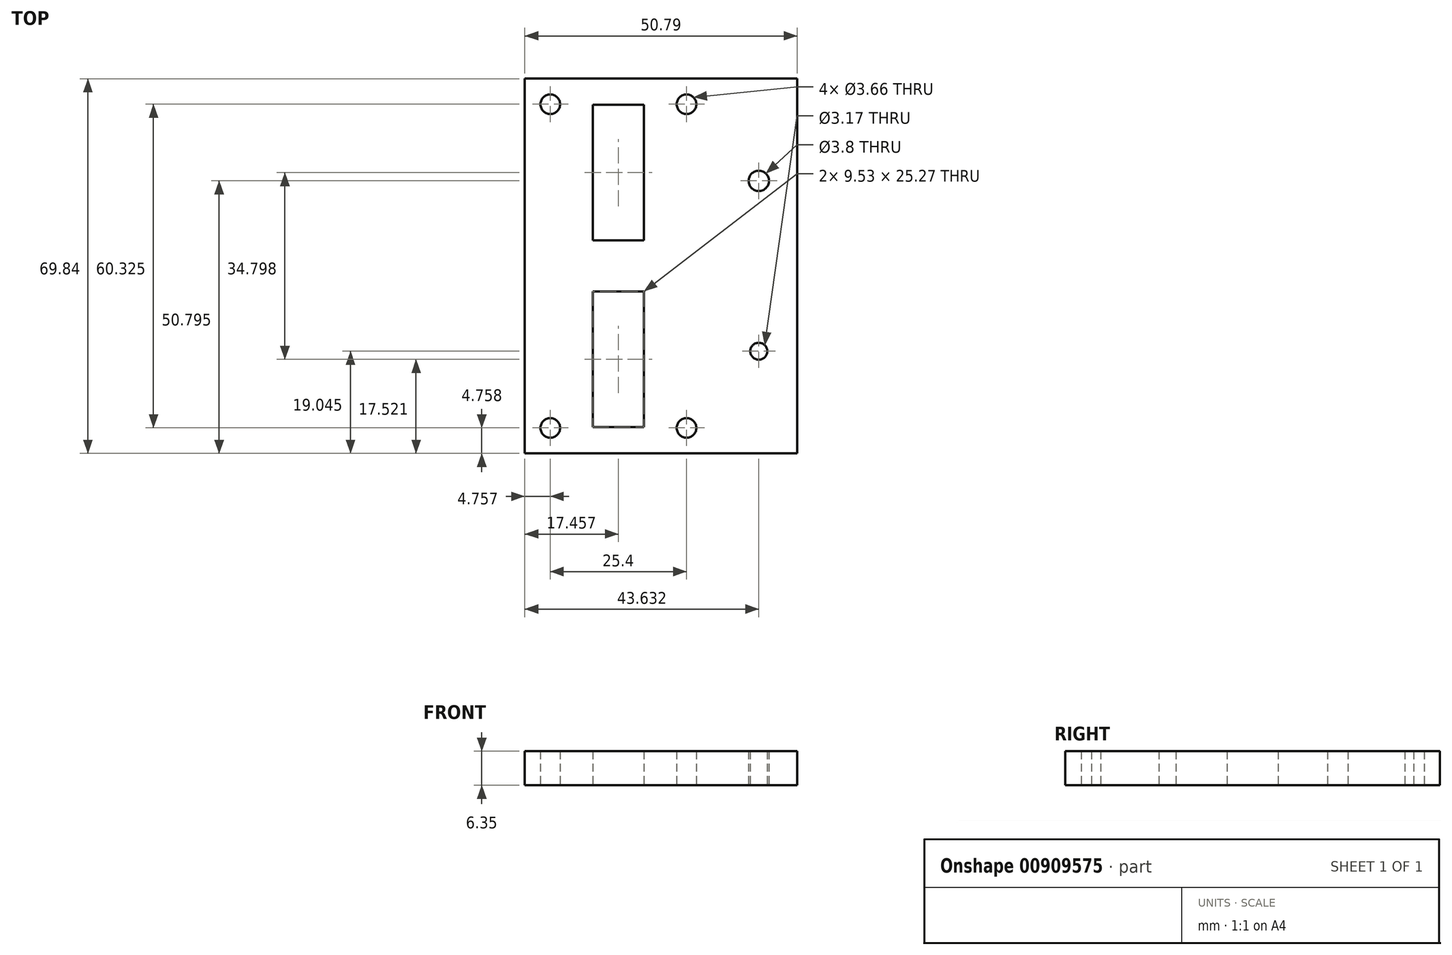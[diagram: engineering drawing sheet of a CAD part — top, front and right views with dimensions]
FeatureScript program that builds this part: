
annotation { "Feature Type Name" : "Feature", "Feature Type Description" : "" }
export const myFeature = defineFeature(function(context is Context, id is Id, definition is map)
    precondition{}
    {
        {
            var Q0;
            Q0=qCreatedBy(makeId("Top.planeOp"),FACE);
            var sketch = newSketch(context, id + "F0", { "sketchPlane" : qUnion([Q0])});
            skLineSegment(sketch, "E0.bottom", {"start": v(-152.4, 152.4) * mm, "end": v(152.4, 152.4) * mm});
            skLineSegment(sketch, "E0.top", {"start": v(-152.4, -152.4) * mm, "end": v(152.4, -152.4) * mm});
            skLineSegment(sketch, "E0.left", {"start": v(-152.4, 152.4) * mm, "end": v(-152.4, -152.4) * mm});
            skLineSegment(sketch, "E0.right", {"start": v(152.4, 152.4) * mm, "end": v(152.4, -152.4) * mm});
            skPoint(sketch, "E0.middle", {"position": v(0, 0) * mm});
            skLineSegment(sketch, "E1.0", {"start": v(-107.95, -82.55) * mm, "end": v(107.95, -82.55) * mm});
            skLineSegment(sketch, "E2.0", {"start": v(-107.95, 107.95) * mm, "end": v(-107.95, -82.55) * mm});
            skLineSegment(sketch, "E3", {"start": v(0, 152.4) * mm, "end": v(0, -152.4) * mm, "construction": true});
            skLineSegment(sketch, "E4", {"start": v(-152.4, 0) * mm, "end": v(152.4, 0) * mm, "construction": true});
            skLineSegment(sketch, "E5.MirrorCS", {"start": v(107.95, 107.95) * mm, "end": v(107.95, -82.55) * mm});
            skLineSegment(sketch, "E6.0", {"start": v(-107.95, 107.95) * mm, "end": v(107.95, 107.95) * mm});
            skLineSegment(sketch, "E7.bottom", {"start": v(-104.78, 34.93) * mm, "end": v(-53.98, 34.93) * mm});
            skLineSegment(sketch, "E7.top", {"start": v(-104.78, -34.92) * mm, "end": v(-53.98, -34.92) * mm});
            skLineSegment(sketch, "E7.left", {"start": v(-104.78, 34.92) * mm, "end": v(-104.78, -34.92) * mm});
            skLineSegment(sketch, "E7.right", {"start": v(-69.85, 34.92) * mm, "end": v(-69.85, -34.92) * mm});
            skLineSegment(sketch, "E8", {"start": v(-87.31, 34.92) * mm, "end": v(-87.31, -152.4) * mm, "construction": true});
            skLineSegment(sketch, "E9.bottom", {"start": v(-82.55, 4.76) * mm, "end": v(-92.08, 4.76) * mm});
            skLineSegment(sketch, "E9.top", {"start": v(-82.55, 30.04) * mm, "end": v(-92.08, 30.04) * mm});
            skLineSegment(sketch, "E9.left", {"start": v(-82.55, 4.76) * mm, "end": v(-82.55, 30.04) * mm});
            skLineSegment(sketch, "E9.right", {"start": v(-92.08, 4.76) * mm, "end": v(-92.08, 30.04) * mm});
            skPoint(sketch, "E9.middle", {"position": v(-87.31, 17.4) * mm});
            skPoint(sketch, "E10", {"position": v(-69.85, 0) * mm});
            skLineSegment(sketch, "E11.MirrorCS", {"start": v(-92.08, -4.76) * mm, "end": v(-92.08, -30.04) * mm});
            skLineSegment(sketch, "E12.MirrorCS", {"start": v(-82.55, -4.76) * mm, "end": v(-82.55, -30.04) * mm});
            skPoint(sketch, "E13.MirrorP", {"position": v(-87.31, -17.4) * mm});
            skLineSegment(sketch, "E14.MirrorCS", {"start": v(-82.55, -4.76) * mm, "end": v(-92.08, -4.76) * mm});
            skLineSegment(sketch, "E15.MirrorCS", {"start": v(-82.55, -30.04) * mm, "end": v(-92.08, -30.04) * mm});
            skCircle(sketch, "E16", {"center": v(-101.6, -127) * mm, "radius": 11.43 * mm});
            skCircle(sketch, "E17", {"center": v(-86.1, -111.5) * mm, "radius": 1.59 * mm});
            skCircle(sketch, "E18.1.0", {"center": v(-117.1, -111.5) * mm, "radius": 1.59 * mm});
            skCircle(sketch, "E18.2.0", {"center": v(-117.1, -142.5) * mm, "radius": 1.59 * mm});
            skCircle(sketch, "E18.3.0", {"center": v(-86.1, -142.5) * mm, "radius": 1.59 * mm});
            skCircle(sketch, "E19.MirrorC", {"center": v(117.1, -111.5) * mm, "radius": 1.59 * mm});
            skCircle(sketch, "E20.MirrorC", {"center": v(86.1, -111.5) * mm, "radius": 1.59 * mm});
            skCircle(sketch, "E21.MirrorC", {"center": v(117.1, -142.5) * mm, "radius": 1.59 * mm});
            skPoint(sketch, "E22.MirrorP", {"position": v(101.6, -127) * mm});
            skCircle(sketch, "E23.MirrorC", {"center": v(86.1, -142.5) * mm, "radius": 1.59 * mm});
            skCircle(sketch, "E24.MirrorC", {"center": v(101.6, -127) * mm, "radius": 11.43 * mm});
            skPoint(sketch, "E25.orphan", {"position": v(-87.31, -34.92) * mm});
            skCircle(sketch, "E26", {"center": v(-103.19, -89.7) * mm, "radius": 1.59 * mm});
            skCircle(sketch, "E27.MirrorC", {"center": v(-71.44, -89.7) * mm, "radius": 1.59 * mm});
            skLineSegment(sketch, "E28.bottom", {"start": v(-96.84, -82.55) * mm, "end": v(-77.79, -82.55) * mm});
            skLineSegment(sketch, "E28.top", {"start": v(-96.84, -96.85) * mm, "end": v(-77.79, -96.85) * mm});
            skLineSegment(sketch, "E28.left", {"start": v(-96.84, -82.55) * mm, "end": v(-96.84, -96.85) * mm});
            skLineSegment(sketch, "E28.right", {"start": v(-77.79, -82.55) * mm, "end": v(-77.79, -96.85) * mm});
            skPoint(sketch, "E29", {"position": v(-87.31, -96.85) * mm});
            skLineSegment(sketch, "E30.MirrorCS", {"start": v(96.84, -82.55) * mm, "end": v(96.84, -96.85) * mm});
            skCircle(sketch, "E31.MirrorC", {"center": v(71.44, -89.7) * mm, "radius": 1.59 * mm});
            skCircle(sketch, "E32.MirrorC", {"center": v(103.19, -89.7) * mm, "radius": 1.59 * mm});
            skLineSegment(sketch, "E33.MirrorCS", {"start": v(96.84, -82.55) * mm, "end": v(77.79, -82.55) * mm});
            skPoint(sketch, "E34.MirrorP", {"position": v(87.31, -96.85) * mm});
            skLineSegment(sketch, "E35.MirrorCS", {"start": v(77.79, -82.55) * mm, "end": v(77.79, -96.85) * mm});
            skLineSegment(sketch, "E36.MirrorCS", {"start": v(96.84, -96.85) * mm, "end": v(77.79, -96.85) * mm});
            skCircle(sketch, "E37.MirrorC", {"center": v(-103.3, 114.85) * mm, "radius": 1.59 * mm});
            skLineSegment(sketch, "E38.MirrorCS", {"start": v(-96.97, 122) * mm, "end": v(-77.92, 122.03) * mm});
            skLineSegment(sketch, "E39.MirrorCS", {"start": v(-96.95, 107.7) * mm, "end": v(-77.9, 107.73) * mm});
            skCircle(sketch, "E40.MirrorC", {"center": v(103.07, 115.1) * mm, "radius": 1.59 * mm});
            skLineSegment(sketch, "E41.MirrorCS", {"start": v(-96.95, 107.7) * mm, "end": v(-96.97, 122) * mm});
            skCircle(sketch, "E42.MirrorC", {"center": v(-71.56, 114.89) * mm, "radius": 1.59 * mm});
            skLineSegment(sketch, "E43.MirrorCS", {"start": v(96.7, 122.24) * mm, "end": v(77.66, 122.21) * mm});
            skCircle(sketch, "E44.MirrorC", {"center": v(71.32, 115.06) * mm, "radius": 1.59 * mm});
            skLineSegment(sketch, "E45.MirrorCS", {"start": v(96.73, 107.94) * mm, "end": v(77.68, 107.91) * mm});
            skPoint(sketch, "E46.MirrorP", {"position": v(-87.44, 122.02) * mm});
            skPoint(sketch, "E47.MirrorP", {"position": v(87.18, 122.23) * mm});
            skLineSegment(sketch, "E48.MirrorCS", {"start": v(-108.06, 107.7) * mm, "end": v(107.84, 107.95) * mm});
            skLineSegment(sketch, "E49.MirrorCS", {"start": v(77.68, 107.91) * mm, "end": v(77.66, 122.21) * mm});
            skLineSegment(sketch, "E50.MirrorCS", {"start": v(-77.9, 107.73) * mm, "end": v(-77.92, 122.03) * mm});
            skLineSegment(sketch, "E51.MirrorCS", {"start": v(96.73, 107.94) * mm, "end": v(96.7, 122.24) * mm});
            skLineSegment(sketch, "E52.0", {"start": v(-53.97, 34.92) * mm, "end": v(-53.98, -34.92) * mm});
            skCircle(sketch, "E53", {"center": v(-61.14, 15.87) * mm, "radius": 1.59 * mm});
            skCircle(sketch, "E54", {"center": v(-100.01, 30.16) * mm, "radius": 1.83 * mm});
            skCircle(sketch, "E55.MirrorC", {"center": v(-100.01, -30.16) * mm, "radius": 1.83 * mm});
            skCircle(sketch, "E56.MirrorC", {"center": v(-74.61, 30.16) * mm, "radius": 1.83 * mm});
            skCircle(sketch, "E57.MirrorC", {"center": v(-74.61, -30.16) * mm, "radius": 1.83 * mm});
            skCircle(sketch, "E58.MirrorC", {"center": v(-61.14, -15.87) * mm, "radius": 1.59 * mm});
            skSolve(sketch);
        }
        {
            var Q0;
            {var subQ1=sQuery(id+"F0.wireOp",EDGE,"E7.right");Q0=makeQuery(id+"F0.imprint","IMPRINT",FACE,{"disambiguationData":[TD([[makeQuery(id+"F0.imprint","IMPRINT",EDGE,{"derivedFrom":subQ1}),1.0]])]});}
            var Q1;
            {var subQ0=sQuery(id+"F0.wireOp",EDGE,"E7.left");Q1=makeQuery(id+"F0.imprint","IMPRINT",FACE,{"disambiguationData":[TD([[makeQuery(id+"F0.imprint","IMPRINT",EDGE,{"derivedFrom":subQ0}),1.0]])]});}
            var Q2;
            Q2=makeQuery(id+"F0.imprint","IMPRINT",FACE,{"disambiguationData":[TD([[makeQuery(id+"F0.imprint","IMPRINT",EDGE,{"derivedFrom":sQuery(id+"F0.wireOp",EDGE,"E55.MirrorC")}),-1.0]])]});
            var Q3;
            Q3=makeQuery(id+"F0.imprint","IMPRINT",FACE,{"disambiguationData":[TD([[makeQuery(id+"F0.imprint","IMPRINT",EDGE,{"derivedFrom":sQuery(id+"F0.wireOp",EDGE,"E54")}),1.0]])]});
            var Q4;
            Q4=makeQuery(id+"F0.imprint","IMPRINT",FACE,{"disambiguationData":[TD([[makeQuery(id+"F0.imprint","IMPRINT",EDGE,{"derivedFrom":sQuery(id+"F0.wireOp",EDGE,"E56.MirrorC")}),-1.0]])]});
            var Q5;
            Q5=makeQuery(id+"F0.imprint","IMPRINT",FACE,{"disambiguationData":[TD([[makeQuery(id+"F0.imprint","IMPRINT",EDGE,{"derivedFrom":sQuery(id+"F0.wireOp",EDGE,"E57.MirrorC")}),1.0]])]});
            var Q6;
            Q6=makeQuery(id+"F0.imprint","IMPRINT",FACE,{"disambiguationData":[TD([[makeQuery(id+"F0.imprint","IMPRINT",EDGE,{"derivedFrom":sQuery(id+"F0.wireOp",EDGE,"E53")}),1.0]])]});
            var Q7;
            Q7=makeQuery(id+"F0.imprint","IMPRINT",FACE,{"disambiguationData":[TD([[makeQuery(id+"F0.imprint","IMPRINT",EDGE,{"derivedFrom":sQuery(id+"F0.wireOp",EDGE,"c3647d2c-fdeb-4a49-b00e-010e5c0727030.MirrorC")}),-1.0]])]});
            var Q8;
            {var subQ3=sQuery(id+"F0.wireOp",EDGE,"E7.right");Q8=makeQuery(id+"F0.imprint","IMPRINT",FACE,{"disambiguationData":[TD([[makeQuery(id+"F0.imprint","IMPRINT",EDGE,{"derivedFrom":subQ3}),-1.0]])]});}
            extrude(context, id + "F1", {"entities" : qUnion([Q0, Q1, Q2, Q3, Q4, Q5, Q6, Q7, Q8]), "depth" : 6.35 * mm, "offsetDistance" : 25.4 * mm});
        }
        {
            var Q0;
            Q0=sQuery(id+"F0.wireOp",VERTEX,"E54.center");
            var Q1;
            Q1=sQuery(id+"F0.wireOp",VERTEX,"E56.MirrorC.center");
            var Q2;
            Q2=sQuery(id+"F0.wireOp",VERTEX,"E57.MirrorC.center");
            var Q3;
            Q3=sQuery(id+"F0.wireOp",VERTEX,"E55.MirrorC.center");
            var Q4;
            Q4=makeQuery(id+"F1.opExtrude","SWEPT_BODY",BODY,{"disambiguationData":[OSD([sQuery(id+"F0.wireOp",EDGE,"E7.bottom"),sQuery(id+"F0.wireOp",EDGE,"E7.top"),sQuery(id+"F0.wireOp",EDGE,"E7.left"),sQuery(id+"F0.wireOp",EDGE,"E9.bottom"),sQuery(id+"F0.wireOp",EDGE,"E9.top"),sQuery(id+"F0.wireOp",EDGE,"E9.left"),sQuery(id+"F0.wireOp",EDGE,"E9.right"),sQuery(id+"F0.wireOp",EDGE,"E11.MirrorCS"),sQuery(id+"F0.wireOp",EDGE,"E12.MirrorCS"),sQuery(id+"F0.wireOp",EDGE,"E14.MirrorCS"),sQuery(id+"F0.wireOp",EDGE,"E15.MirrorCS"),sQuery(id+"F0.wireOp",EDGE,"E52.0")])]});
            hole(context, id + "F2", {"style" : HoleStyle.SIMPLE, "endStyle" : HoleEndStyle.THROUGH, "oppositeDirection" : true, "standardTappedOrClearance" : lookupTablePath({ "fit" : "Close", "standard" : "ANSI", "size" : "#6", "type" : "Clearance" }), "standardBlindInLast" : lookupTablePath({ "fit" : "Close", "standard" : "ANSI", "size" : "#6", "type" : "Clearance" }), "holeDiameter" : 3.66 * mm, "majorDiameter" : 6.35 * mm, "isTappedThrough" : true, "tappedDepth" : 12.7 * mm, "tapClearance" : 3, "locations" : qUnion([Q0, Q1, Q2, Q3]), "scope" : qUnion([Q4])});
        }
        {
            var Q0;
            Q0=sQuery(id+"F0.wireOp",VERTEX,"c3647d2c-fdeb-4a49-b00e-010e5c0727030.MirrorC.center");
            var Q1;
            Q1=sQuery(id+"F0.wireOp",VERTEX,"E53.center");
            var Q2;
            Q2=makeQuery(id+"F1.opExtrude","SWEPT_BODY",BODY,{"disambiguationData":[OSD([sQuery(id+"F0.wireOp",EDGE,"E7.bottom"),sQuery(id+"F0.wireOp",EDGE,"E7.top"),sQuery(id+"F0.wireOp",EDGE,"E7.left"),sQuery(id+"F0.wireOp",EDGE,"E9.bottom"),sQuery(id+"F0.wireOp",EDGE,"E9.top"),sQuery(id+"F0.wireOp",EDGE,"E9.left"),sQuery(id+"F0.wireOp",EDGE,"E9.right"),sQuery(id+"F0.wireOp",EDGE,"E11.MirrorCS"),sQuery(id+"F0.wireOp",EDGE,"E12.MirrorCS"),sQuery(id+"F0.wireOp",EDGE,"E14.MirrorCS"),sQuery(id+"F0.wireOp",EDGE,"E15.MirrorCS"),sQuery(id+"F0.wireOp",EDGE,"E52.0")])]});
            hole(context, id + "F3", {"style" : HoleStyle.SIMPLE, "endStyle" : HoleEndStyle.THROUGH, "oppositeDirection" : true, "standardTappedOrClearance" : lookupTablePath({ "fit" : "Normal (ASME)", "standard" : "ANSI", "size" : "#6", "type" : "Clearance" }), "standardBlindInLast" : lookupTablePath({ "fit" : "Free", "standard" : "ANSI", "size" : "#6", "type" : "Clearance" }), "holeDiameter" : 3.8 * mm, "majorDiameter" : 3.5 * mm, "isTappedThrough" : true, "tappedDepth" : 12.7 * mm, "tapClearance" : 3, "locations" : qUnion([Q0, Q1]), "scope" : qUnion([Q2])});
        }
    });
